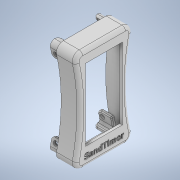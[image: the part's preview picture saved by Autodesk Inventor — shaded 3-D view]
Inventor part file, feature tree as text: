
AUTODESK INVENTOR PART (.ipt)
format: ipt  version: 2021 (Build 250183000, 183)  size: 651,776 bytes
history: native  units: mm
features: extrude x7, sketch x7, fillet x4, projected_geometry x4, plane x3, mirror x2, shell x1
ambient origin geometry x8: Origin, YZ Plane, XZ Plane, XY Plane, X Axis, Y Axis, Z Axis, Center Point
bodies: Solid1 (feature_tree)
feature tree (28):
  extrude  "Extrusion1"  Depth=27.0mm
  extrude  "Extrusion5"  Depth=1.5mm
  fillet  "Fillet1"  Radius=1.5mm
  shell  "Shell1"  Thickness=3.8mm
  extrude  "Extrusion9"  Depth=4.0mm
  extrude  "Extrusion12"  Depth=41.0mm
  plane  "Work Plane1"
  extrude  "Extrusion14"  TaperAngle=0.0deg  [1 undecoded]
  plane  "Work Plane4"
  extrude  "Extrusion15"  Depth=24.0mm
  fillet  "Fillet10"  Radius=4.0mm
  fillet  "Fillet11"  Radius=3.0mm
  mirror  "Mirror5"
  plane  "Work Plane5"
  mirror  "Mirror6"
  extrude  "Extrusion16"  Depth=1.5mm
  fillet  "Fillet12"  Radius=2.0mm
  sketch  "Sketch1"  dims[d0=11.0mm d1=27.0mm]
  sketch  "Sketch5"  dims[d2=58.0mm d3=0.0mm d4=2.0mm d5=1.5mm d26=3.8mm]
  sketch  "Sketch9"  dims[d27=0.0mm d28=0.0mm d29=4.0mm]
  sketch  "Sketch12"  dims[d53=21.0mm d54=41.0mm]
  sketch  "Sketch14"  dims[d55=6.54mm d56=0.0mm d57=0.0mm]
  sketch  "Sketch15"  dims[d58=-3.0mm d68=24.0mm d69=4.0mm d70=3.0mm]
  sketch  "Sketch16"  dims[d71=0.5mm d72=0.0mm d83=1.5mm d84=2.0mm d87=8.0mm d88=0.0mm d89=2.4mm d90=2.5mm d92=0.0mm d93=0.0mm d94=2.0mm d95=0.5mm d97=2.5mm d98=5.0mm d99=1.0mm d100=1.7mm d101=4.0mm d102=0.0mm d103=1.7mm d104=0.25mm d105=1.0mm]
  projected_geometry  "Project Cut Edges8"
  projected_geometry  "Project Cut Edges9"
  projected_geometry  "Project Cut Edges10"
  projected_geometry  "Project Cut Edges11"
note: 1 required parameter value undecoded (feature->parameter linkage not recoverable at this tier; creation-order binding heuristic only, values carry confidence <= 0.55)
